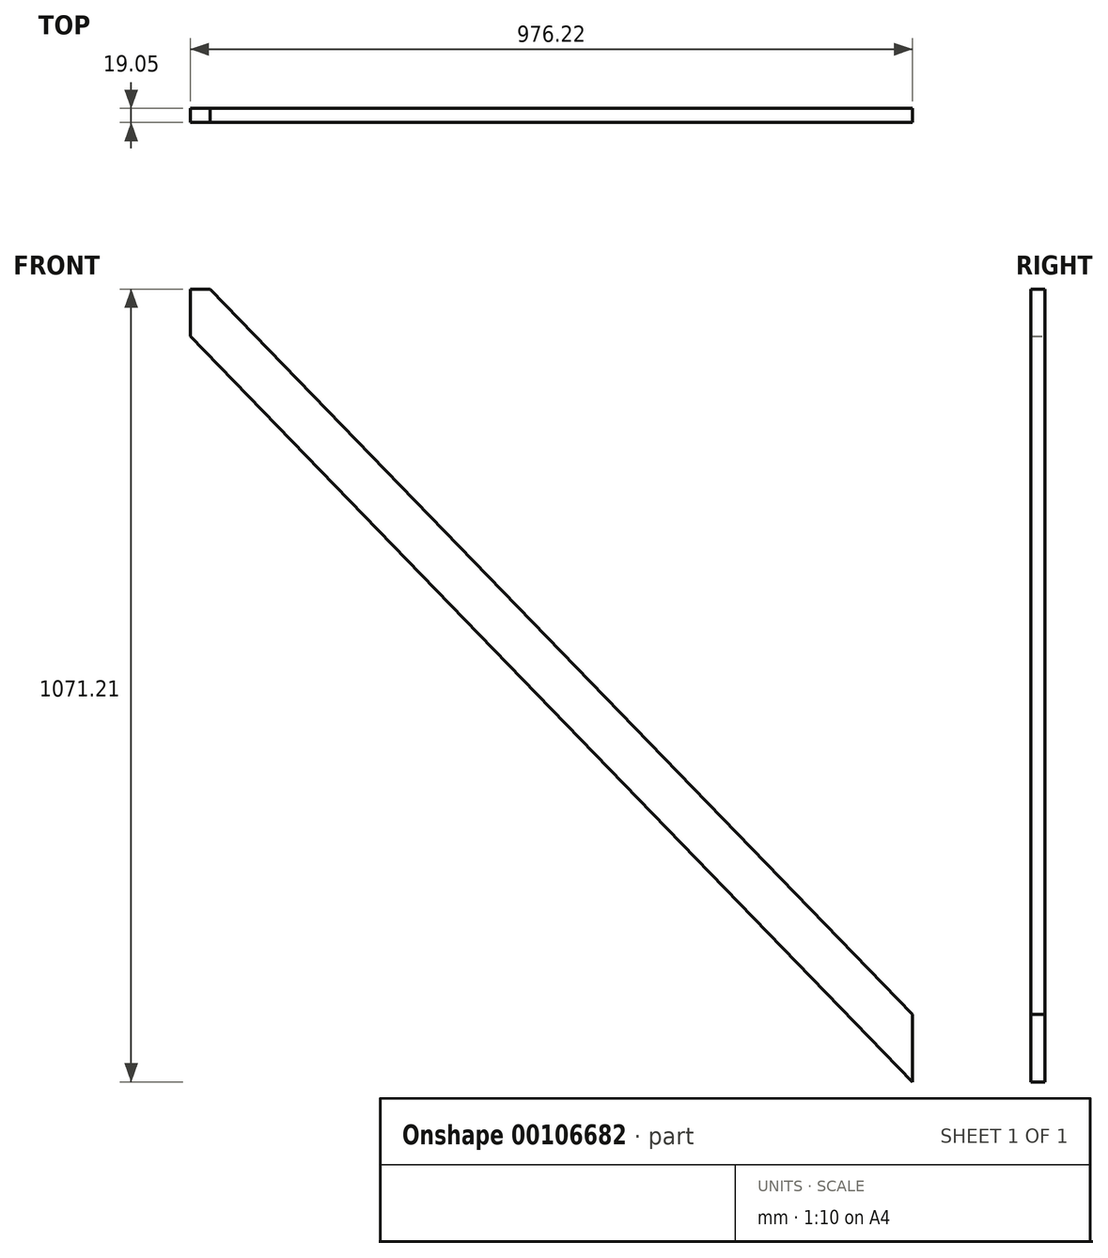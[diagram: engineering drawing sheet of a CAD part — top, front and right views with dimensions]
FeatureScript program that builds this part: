
annotation { "Feature Type Name" : "Feature", "Feature Type Description" : "" }
export const myFeature = defineFeature(function(context is Context, id is Id, definition is map)
    precondition{}
    {
        {
            var Q0;
            Q0=qCreatedBy(makeId("Front.planeOp"),FACE);
            var sketch = newSketch(context, id + "F0", { "sketchPlane" : qUnion([Q0])});
            skLineSegment(sketch, "E0", {"start": v(-189.46, 269.74) * mm, "end": v(-189.46, 178.48) * mm});
            skLineSegment(sketch, "E1", {"start": v(-189.46, 178.48) * mm, "end": v(759.87, -801.47) * mm});
            skLineSegment(sketch, "E2", {"start": v(759.87, -801.47) * mm, "end": v(759.87, -710.2) * mm});
            skLineSegment(sketch, "E3", {"start": v(759.87, -710.2) * mm, "end": v(-189.46, 269.74) * mm});
            skLineSegment(sketch, "E4", {"start": v(-189.46, 269.74) * mm, "end": v(-216.35, 269.74) * mm});
            skLineSegment(sketch, "E5", {"start": v(-189.46, 178.48) * mm, "end": v(-216.35, 206.24) * mm});
            skLineSegment(sketch, "E6", {"start": v(-216.35, 269.74) * mm, "end": v(-216.35, 206.24) * mm});
            skSolve(sketch);
        }
        {
            var Q0;
            Q0=makeQuery(id+"F0.imprint","IMPRINT",FACE,{"disambiguationData":[TD([[makeQuery(id+"F0.imprint","IMPRINT",EDGE,{"derivedFrom":sQuery(id+"F0.wireOp",EDGE,"E0")}),1.0]])]});
            var Q1;
            Q1=makeQuery(id+"F0.imprint","IMPRINT",FACE,{"disambiguationData":[TD([[makeQuery(id+"F0.imprint","IMPRINT",EDGE,{"derivedFrom":sQuery(id+"F0.wireOp",EDGE,"E0")}),-1.0]])]});
            extrude(context, id + "F1", {"entities" : qUnion([Q0, Q1]), "depth" : 19.05 * mm});
        }
    });
